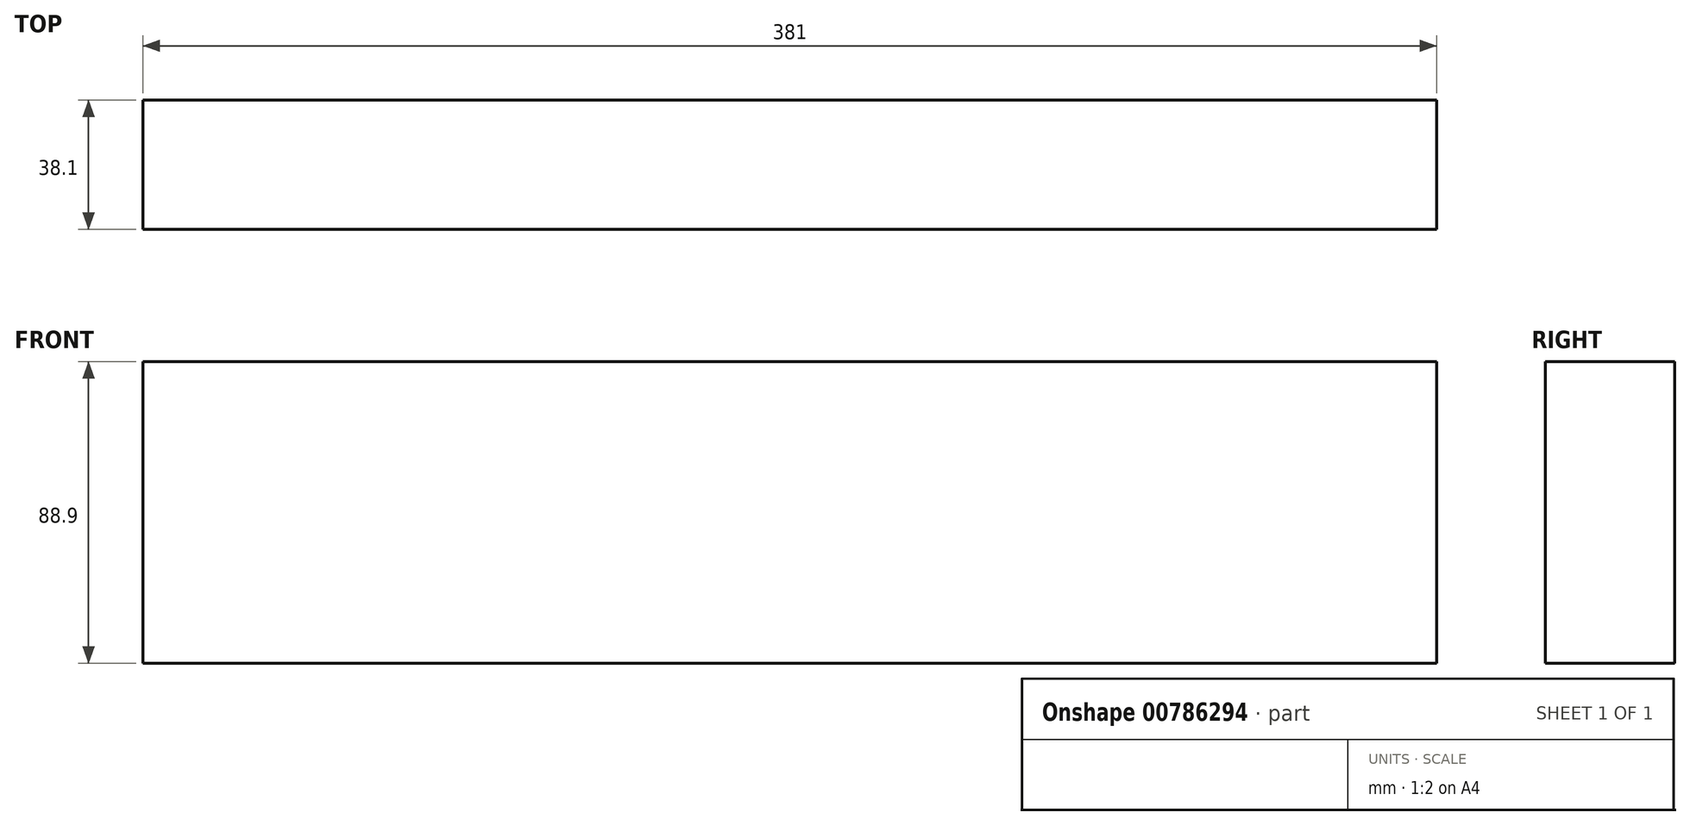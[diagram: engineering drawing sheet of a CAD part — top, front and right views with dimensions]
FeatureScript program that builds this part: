
annotation { "Feature Type Name" : "Feature", "Feature Type Description" : "" }
export const myFeature = defineFeature(function(context is Context, id is Id, definition is map)
    precondition{}
    {
        {
            var Q0;
            Q0=qCreatedBy(makeId("Front.planeOp"),FACE);
            var sketch = newSketch(context, id + "F0", { "sketchPlane" : qUnion([Q0])});
            skLineSegment(sketch, "E0.bottom", {"start": v(-190.5, 44.45) * mm, "end": v(190.5, 44.45) * mm});
            skLineSegment(sketch, "E0.top", {"start": v(-190.5, -44.45) * mm, "end": v(190.5, -44.45) * mm});
            skLineSegment(sketch, "E0.left", {"start": v(-190.5, 44.45) * mm, "end": v(-190.5, -44.45) * mm});
            skLineSegment(sketch, "E0.right", {"start": v(190.5, 44.45) * mm, "end": v(190.5, -44.45) * mm});
            skPoint(sketch, "E0.middle", {"position": v(0, 0) * mm});
            skSolve(sketch);
        }
        {
            var Q0;
            Q0 = qSketchRegion(id + "F0", true);
            extrude(context, id + "F1", {"entities" : qUnion([Q0]), "endBound" : BoundingType.SYMMETRIC, "depth" : 38.1 * mm, "offsetDistance" : 25.4 * mm});
        }
    });
